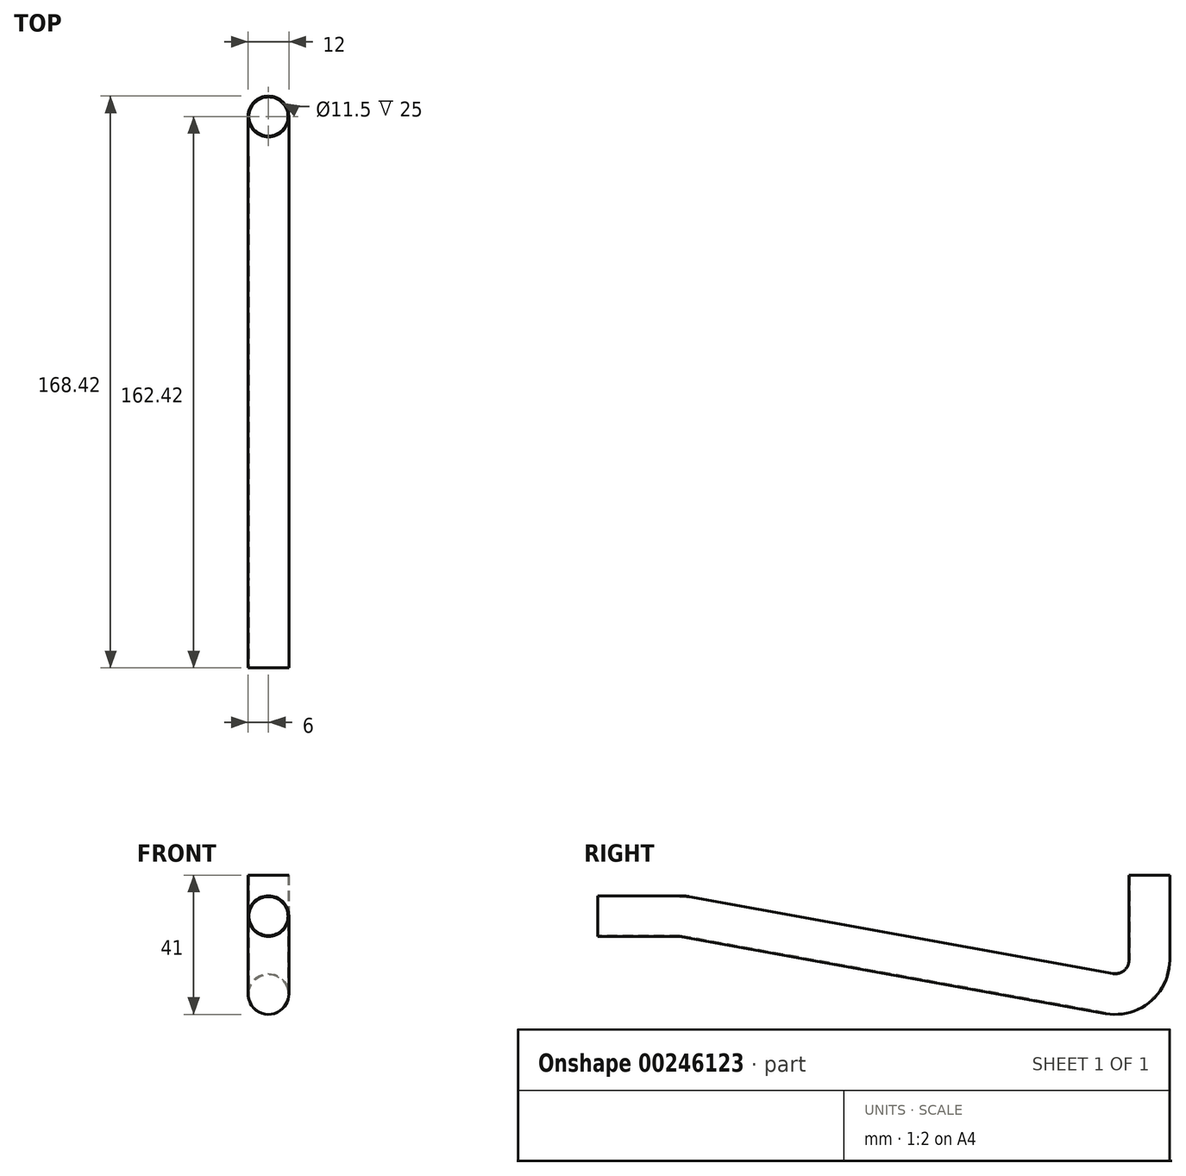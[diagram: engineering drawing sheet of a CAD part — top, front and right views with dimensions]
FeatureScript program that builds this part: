
annotation { "Feature Type Name" : "Feature", "Feature Type Description" : "" }
export const myFeature = defineFeature(function(context is Context, id is Id, definition is map)
    precondition{}
    {
        {
            var Q0;
            Q0=qCreatedBy(makeId("Right.planeOp"),FACE);
            var sketch = newSketch(context, id + "F0", { "sketchPlane" : qUnion([Q0])});
            skLineSegment(sketch, "E0", {"start": v(-162.42, 5.11) * mm, "end": v(0, 0) * mm});
            skLineSegment(sketch, "E1", {"start": v(-162.42, -12.07) * mm, "end": v(-138.32, -12.07) * mm});
            skLineSegment(sketch, "E2", {"start": v(-136.54, -12.23) * mm, "end": v(-11.78, -34.84) * mm});
            skPoint(sketch, "E3.visualSharp", {"position": v(-137.42, -12.07) * mm});
            skArc(sketch, "E3.filletArc", {"start": v(-136.54, -12.23) * mm, "mid": v(-137.42, -12.11) * mm, "end": v(-138.32, -12.07) * mm});
            skLineSegment(sketch, "E4", {"start": v(0, -25) * mm, "end": v(0, 0) * mm});
            skPoint(sketch, "E5.visualSharp", {"position": v(0, 0) * mm});
            skArc(sketch, "E5.filletArc", {"start": v(-11.78, -34.84) * mm, "mid": v(-3.6, -32.68) * mm, "end": v(0, -25) * mm});
            skLineSegment(sketch, "E6", {"start": v(0, 0) * mm, "end": v(-6, 0) * mm});
            skLineSegment(sketch, "E7", {"start": v(-162.42, -6.07) * mm, "end": v(-162.42, -18.07) * mm});
            skLineSegment(sketch, "E8", {"start": v(-162.42, -6.07) * mm, "end": v(-137.42, -6.07) * mm});
            skLineSegment(sketch, "E9", {"start": v(-162.42, -18.07) * mm, "end": v(-138.32, -18.07) * mm});
            skLineSegment(sketch, "E10", {"start": v(-136.54, -18.23) * mm, "end": v(-8.14, -41.5) * mm});
            skLineSegment(sketch, "E11", {"start": v(-137.42, -6.07) * mm, "end": v(-15.43, -28.18) * mm});
            skLineSegment(sketch, "E12", {"start": v(-6, -20.3) * mm, "end": v(-6, 0) * mm});
            skLineSegment(sketch, "E13", {"start": v(6, -29.7) * mm, "end": v(6, 0) * mm});
            skLineSegment(sketch, "E14", {"start": v(6, 0) * mm, "end": v(-6, 0) * mm});
            skPoint(sketch, "E15.visualSharp", {"position": v(-6, -29.89) * mm});
            skArc(sketch, "E15.filletArc", {"start": v(-15.43, -28.18) * mm, "mid": v(-8.87, -26.45) * mm, "end": v(-6, -20.3) * mm});
            skPoint(sketch, "E16.visualSharp", {"position": v(6, -44.06) * mm});
            skArc(sketch, "E16.filletArc", {"start": v(-8.14, -41.5) * mm, "mid": v(1.7, -38.9) * mm, "end": v(6, -29.7) * mm});
            skPoint(sketch, "E17.visualSharp", {"position": v(-137.42, -18.07) * mm});
            skArc(sketch, "E17.filletArc", {"start": v(-136.54, -18.23) * mm, "mid": v(-137.42, -18.11) * mm, "end": v(-138.32, -18.07) * mm});
            skLineSegment(sketch, "E18", {"start": v(0, -25) * mm, "end": v(-194.16, -25) * mm});
            skSolve(sketch);
        }
        {
            var Q0;
            Q0=qCreatedBy(makeId("Top.planeOp"),FACE);
            var sketch = newSketch(context, id + "F1", { "sketchPlane" : qUnion([Q0])});
            skCircle(sketch, "E19", {"center": v(0, 0) * mm, "radius": 6 * mm});
            skCircle(sketch, "E20", {"center": v(0, 0) * mm, "radius": 5.75 * mm});
            skSolve(sketch);
        }
        {
            var Q0;
            Q0=makeQuery(id+"F1.imprint","IMPRINT",FACE,{"disambiguationData":[TD([[makeQuery(id+"F1.imprint","IMPRINT",EDGE,{"derivedFrom":sQuery(id+"F1.wireOp",EDGE,"E19")}),1.0]])]});
            var Q1;
            Q1=sQuery(id+"F0.wireOp",EDGE,"E4");
            var Q2;
            Q2=sQuery(id+"F0.wireOp",EDGE,"E5.filletArc");
            var Q3;
            Q3=sQuery(id+"F0.wireOp",EDGE,"E2");
            var Q4;
            Q4=sQuery(id+"F0.wireOp",EDGE,"E1");
            var Q5;
            Q5=sQuery(id+"F0.wireOp",EDGE,"E3.filletArc");
            sweep(context, id + "F2", {"profiles" : qUnion([Q0]), "path" : qUnion([Q1, Q2, Q3, Q4, Q5])});
        }
    });
